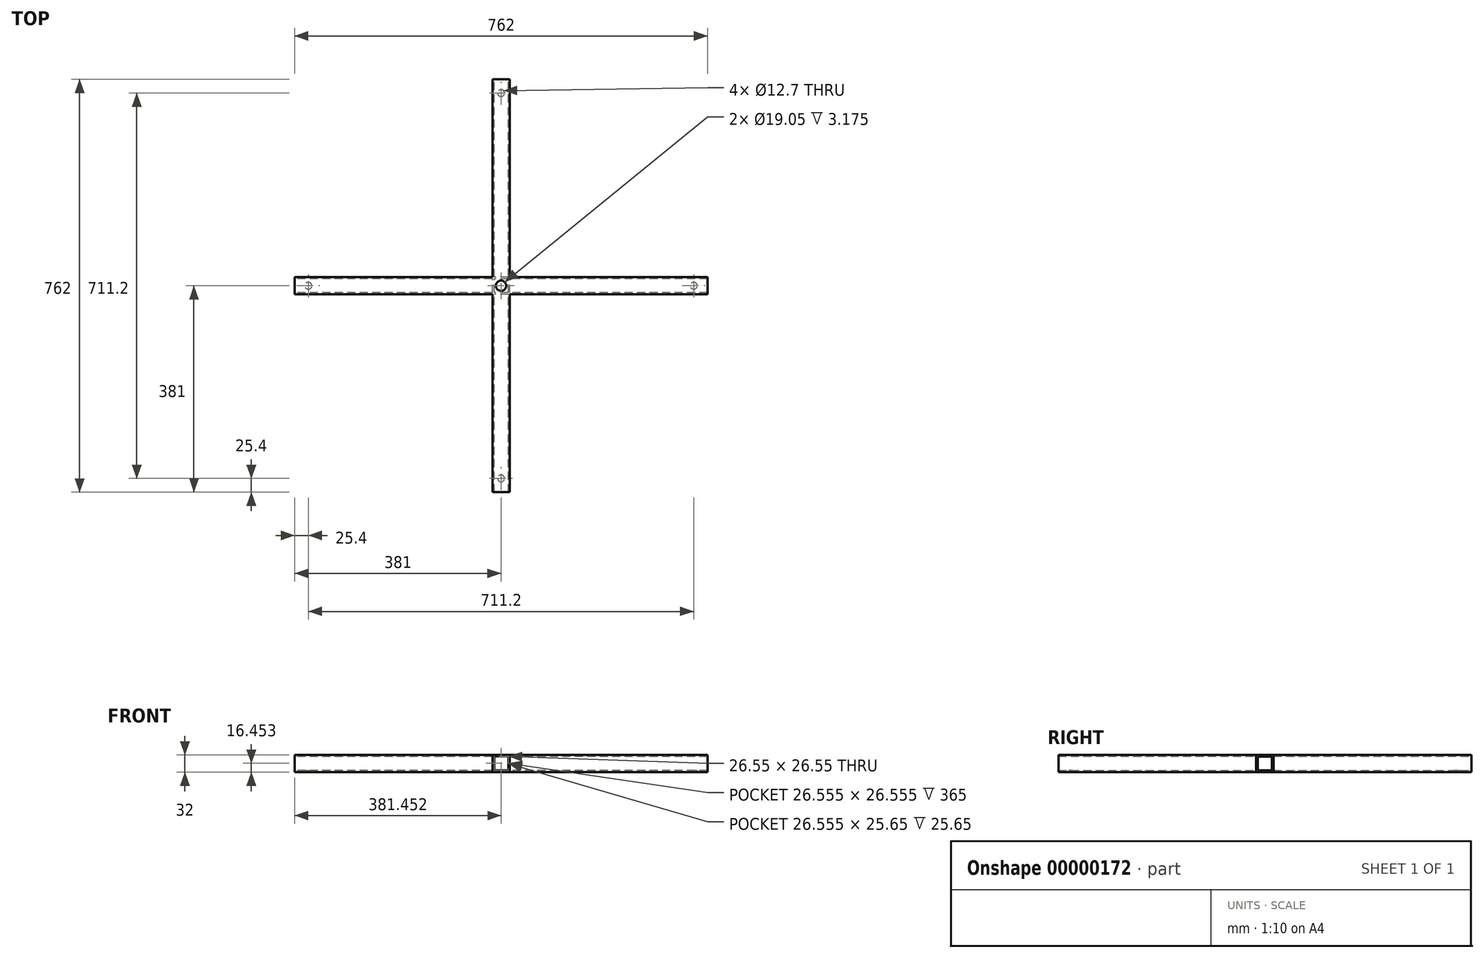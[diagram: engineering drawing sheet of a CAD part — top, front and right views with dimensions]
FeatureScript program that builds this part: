
annotation { "Feature Type Name" : "Feature", "Feature Type Description" : "" }
export const myFeature = defineFeature(function(context is Context, id is Id, definition is map)
    precondition{}
    {
        {
            var Q0;
            Q0=qCreatedBy(makeId("Front.planeOp"),FACE);
            var sketch = newSketch(context, id + "F0", { "sketchPlane" : qUnion([Q0])});
            skLineSegment(sketch, "E0.bottom", {"start": v(-16, 16) * mm, "end": v(16, 16) * mm});
            skLineSegment(sketch, "E0.top", {"start": v(-16, -16) * mm, "end": v(16, -16) * mm});
            skLineSegment(sketch, "E0.left", {"start": v(-16, 16) * mm, "end": v(-16, -16) * mm});
            skLineSegment(sketch, "E0.right", {"start": v(16, 16) * mm, "end": v(16, -16) * mm});
            skLineSegment(sketch, "E1", {"start": v(-16, 0) * mm, "end": v(16, 0) * mm, "construction": true});
            skLineSegment(sketch, "E2", {"start": v(0, 16) * mm, "end": v(0, -16) * mm, "construction": true});
            skLineSegment(sketch, "E3.bottom", {"start": v(-12.83, 13.73) * mm, "end": v(13.73, 13.73) * mm});
            skLineSegment(sketch, "E3.top", {"start": v(-12.82, -12.82) * mm, "end": v(13.73, -12.82) * mm});
            skLineSegment(sketch, "E3.left", {"start": v(-12.83, 13.73) * mm, "end": v(-12.82, -12.82) * mm});
            skLineSegment(sketch, "E3.right", {"start": v(13.73, 13.73) * mm, "end": v(13.73, -12.82) * mm});
            skSolve(sketch);
        }
        {
            var Q0;
            Q0=makeQuery(id+"F0.imprint","IMPRINT",FACE,{"disambiguationData":[TD([[makeQuery(id+"F0.imprint","IMPRINT",EDGE,{"derivedFrom":sQuery(id+"F0.wireOp",EDGE,"E0.bottom")}),-1.0]])]});
            extrude(context, id + "F1", {"entities" : qUnion([Q0]), "depth" : 762 * mm, "symmetric" : true});
        }
        {
            var Q0;
            Q0=qCreatedBy(makeId("Right.planeOp"),FACE);
            var sketch = newSketch(context, id + "F2", { "sketchPlane" : qUnion([Q0])});
            skLineSegment(sketch, "E4.bottom", {"start": v(16, 16) * mm, "end": v(-16, 16) * mm});
            skLineSegment(sketch, "E4.top", {"start": v(16, -16) * mm, "end": v(-16, -16) * mm});
            skLineSegment(sketch, "E4.left", {"start": v(16, 16) * mm, "end": v(16, -16) * mm});
            skLineSegment(sketch, "E4.right", {"start": v(-16, 16) * mm, "end": v(-16, -16) * mm});
            skLineSegment(sketch, "E5.bottom", {"start": v(12.83, 12.83) * mm, "end": v(-12.83, 12.82) * mm});
            skLineSegment(sketch, "E5.top", {"start": v(12.83, -12.82) * mm, "end": v(-12.83, -12.83) * mm});
            skLineSegment(sketch, "E5.left", {"start": v(12.83, 12.83) * mm, "end": v(12.83, -12.82) * mm});
            skLineSegment(sketch, "E5.right", {"start": v(-12.83, 12.82) * mm, "end": v(-12.83, -12.83) * mm});
            skLineSegment(sketch, "E6", {"start": v(16, 0) * mm, "end": v(-16, 0) * mm, "construction": true});
            skSolve(sketch);
        }
        {
            var Q0;
            Q0=makeQuery(id+"F2.imprint","IMPRINT",FACE,{"disambiguationData":[TD([[makeQuery(id+"F2.imprint","IMPRINT",EDGE,{"derivedFrom":sQuery(id+"F2.wireOp",EDGE,"E4.bottom")}),1.0]])]});
            extrude(context, id + "F3", {"entities" : qUnion([Q0]), "operationType" : NewBodyOperationType.ADD, "depth" : 762 * mm, "symmetric" : true});
        }
        {
            var Q0;
            Q0=qCreatedBy(makeId("Top.planeOp"),FACE);
            var sketch = newSketch(context, id + "F4", { "sketchPlane" : qUnion([Q0])});
            skCircle(sketch, "E7", {"center": v(0, 0) * mm, "radius": 9.53 * mm});
            skSolve(sketch);
        }
        {
            var Q0;
            Q0=makeQuery(id+"F4.imprint","IMPRINT",FACE,{"disambiguationData":[TD([[makeQuery(id+"F4.imprint","IMPRINT",EDGE,{"derivedFrom":sQuery(id+"F4.wireOp",EDGE,"E7")}),1.0]])]});
            extrude(context, id + "F5", {"entities" : qUnion([Q0]), "operationType" : NewBodyOperationType.REMOVE, "oppositeDirection" : true, "depth" : 50 * mm, "symmetric" : true});
        }
        {
            var Q0;
            Q0=makeQuery(id+"F3.boolean.opBoolean","MERGE",FACE,{"derivedFrom":[makeQuery(id+"F1.opExtrude","SWEPT_FACE",FACE,{"disambiguationData":[OSD([sQuery(id+"F0.wireOp",EDGE,"E0.top")])]}),makeQuery(id+"F3.opExtrude","SWEPT_FACE",FACE,{"disambiguationData":[OSD([sQuery(id+"F2.wireOp",EDGE,"E4.top")])]})]});
            var sketch = newSketch(context, id + "F6", { "sketchPlane" : qUnion([Q0])});
            skLineSegment(sketch, "E8", {"start": v(-381, 0) * mm, "end": v(381, 0) * mm, "construction": true});
            skLineSegment(sketch, "E9", {"start": v(0, 381) * mm, "end": v(0, -381) * mm, "construction": true});
            skCircle(sketch, "E10", {"center": v(-355.6, 0) * mm, "radius": 6.35 * mm});
            skCircle(sketch, "E11", {"center": v(355.6, 0) * mm, "radius": 6.35 * mm});
            skCircle(sketch, "E12", {"center": v(0, 355.6) * mm, "radius": 6.35 * mm});
            skCircle(sketch, "E13", {"center": v(0, -355.6) * mm, "radius": 6.35 * mm});
            skSolve(sketch);
        }
        {
            var Q0;
            {Q0=qUnion([makeQuery(id+"F6.imprint","IMPRINT",FACE,{"disambiguationData":[TD([[makeQuery(id+"F6.imprint","IMPRINT",EDGE,{"derivedFrom":sQuery(id+"F6.wireOp",EDGE,"E10")}),1.0]])]}),makeQuery(id+"F6.imprint","IMPRINT",FACE,{"disambiguationData":[TD([[makeQuery(id+"F6.imprint","IMPRINT",EDGE,{"derivedFrom":sQuery(id+"F6.wireOp",EDGE,"E11")}),1.0]])]}),makeQuery(id+"F6.imprint","IMPRINT",FACE,{"disambiguationData":[TD([[makeQuery(id+"F6.imprint","IMPRINT",EDGE,{"derivedFrom":sQuery(id+"F6.wireOp",EDGE,"E12")}),1.0]])]}),makeQuery(id+"F6.imprint","IMPRINT",FACE,{"disambiguationData":[TD([[makeQuery(id+"F6.imprint","IMPRINT",EDGE,{"derivedFrom":sQuery(id+"F6.wireOp",EDGE,"E13")}),1.0]])]})]);}
            extrude(context, id + "F7", {"entities" : qUnion([Q0]), "operationType" : NewBodyOperationType.REMOVE, "endBound" : BoundingType.UP_TO_NEXT, "oppositeDirection" : true, "depth" : 25 * mm});
        }
    });
